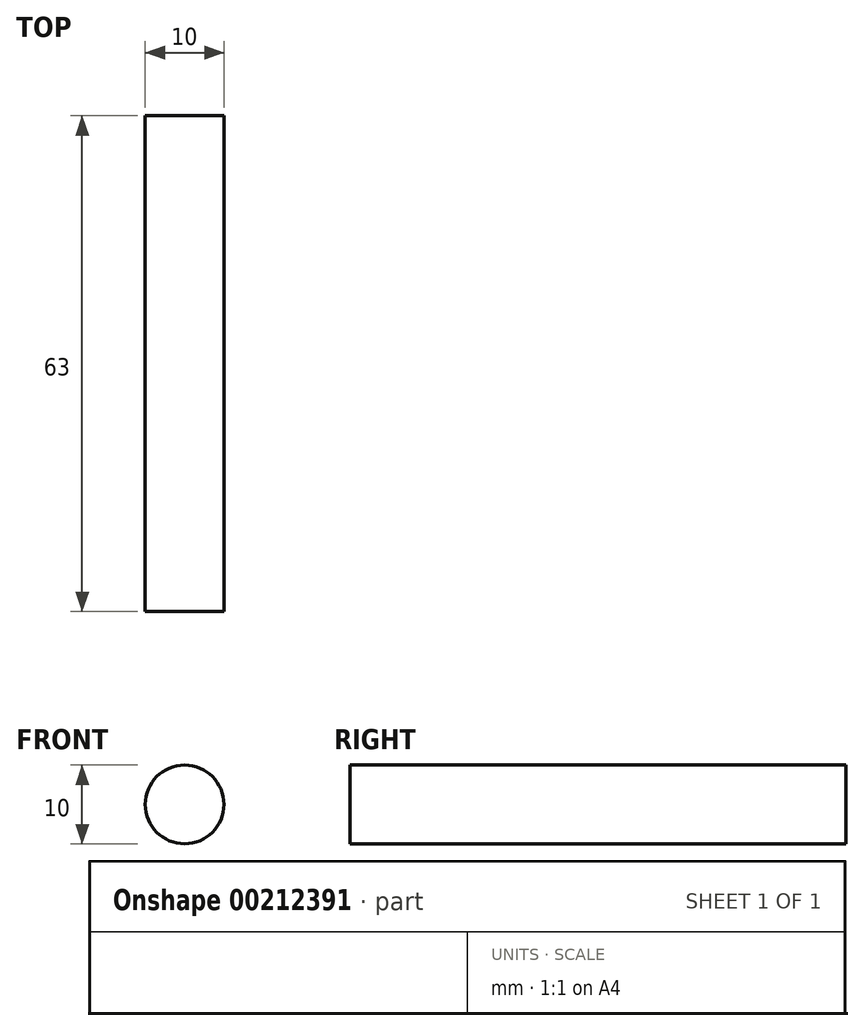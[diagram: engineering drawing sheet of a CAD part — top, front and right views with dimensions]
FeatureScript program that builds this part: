
annotation { "Feature Type Name" : "Feature", "Feature Type Description" : "" }
export const myFeature = defineFeature(function(context is Context, id is Id, definition is map)
    precondition{}
    {
        {
            var Q0;
            Q0=qCreatedBy(makeId("Front.planeOp"),FACE);
            var sketch = newSketch(context, id + "F0", { "sketchPlane" : qUnion([Q0])});
            skCircle(sketch, "E0", {"center": v(0, 0) * mm, "radius": 5 * mm});
            skSolve(sketch);
        }
        {
            var Q0;
            Q0=makeQuery(id+"F0.imprint","IMPRINT",FACE,{"disambiguationData":[TD([[makeQuery(id+"F0.imprint","IMPRINT",EDGE,{"derivedFrom":sQuery(id+"F0.wireOp",EDGE,"E0")}),1.0]])]});
            extrude(context, id + "F1", {"entities" : qUnion([Q0]), "depth" : 63 * mm});
        }
    });
